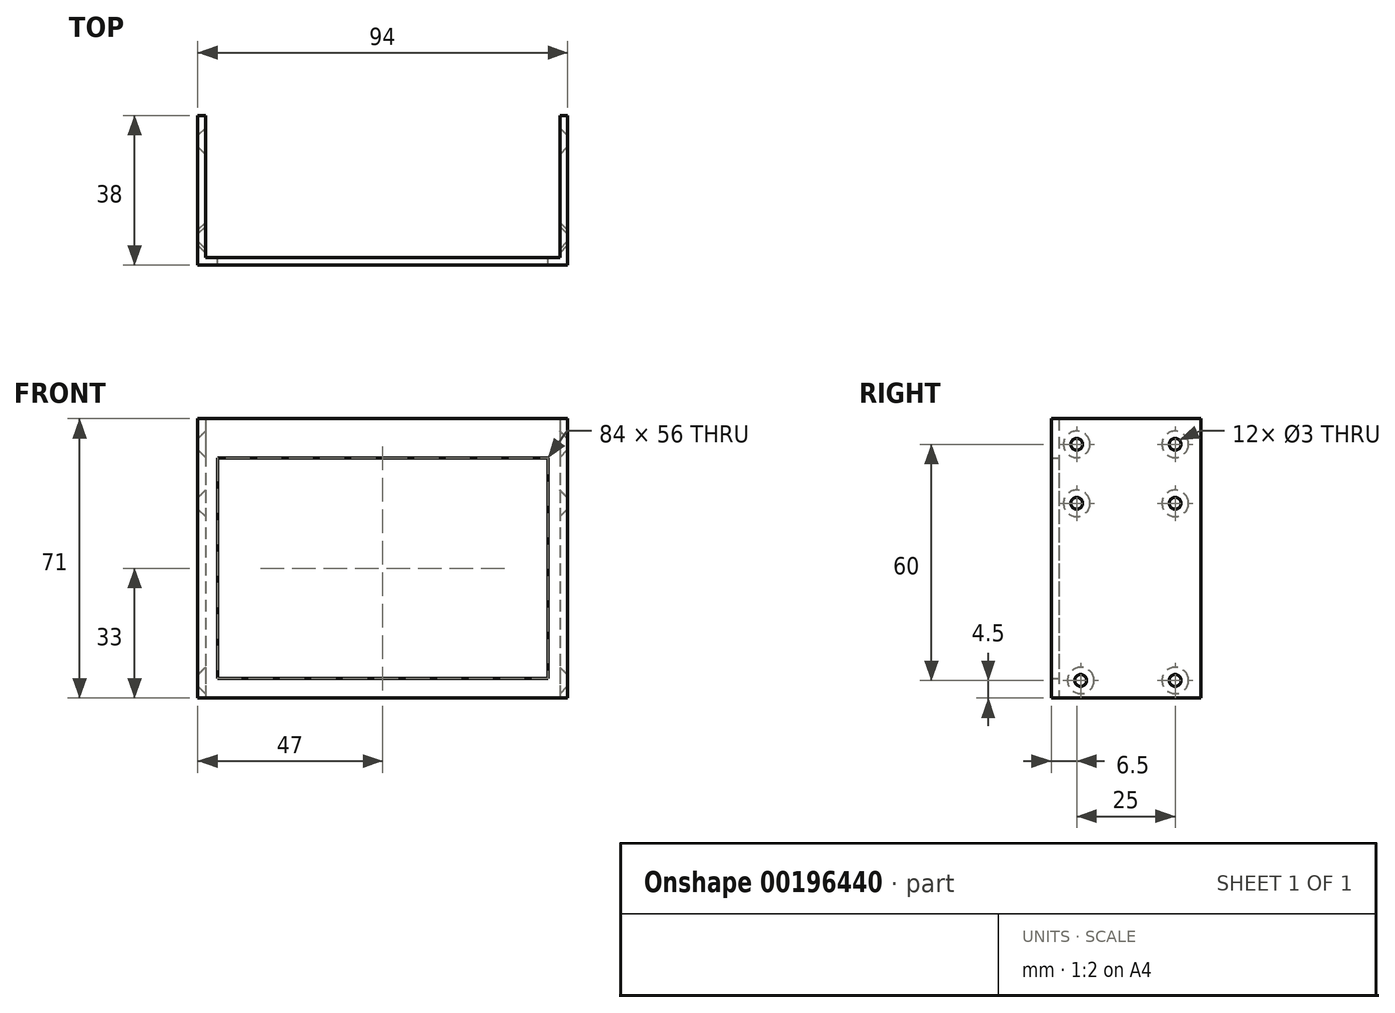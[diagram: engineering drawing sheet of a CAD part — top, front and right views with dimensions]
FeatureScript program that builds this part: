
annotation { "Feature Type Name" : "Feature", "Feature Type Description" : "" }
export const myFeature = defineFeature(function(context is Context, id is Id, definition is map)
    precondition{}
    {
        {
            var Q0;
            Q0=qCreatedBy(makeId("Front.planeOp"),FACE);
            var sketch = newSketch(context, id + "F0", { "sketchPlane" : qUnion([Q0])});
            skLineSegment(sketch, "E0.bottom", {"start": v(47, 35.5) * mm, "end": v(-47, 35.5) * mm});
            skLineSegment(sketch, "E0.top", {"start": v(47, -35.5) * mm, "end": v(-47, -35.5) * mm});
            skLineSegment(sketch, "E0.left", {"start": v(47, 35.5) * mm, "end": v(47, -35.5) * mm});
            skLineSegment(sketch, "E0.right", {"start": v(-47, 35.5) * mm, "end": v(-47, -35.5) * mm});
            skPoint(sketch, "E0.middle", {"position": v(0, 0) * mm});
            skLineSegment(sketch, "E1.bottom", {"start": v(42, 25.5) * mm, "end": v(-42, 25.5) * mm});
            skLineSegment(sketch, "E1.top", {"start": v(42, -30.5) * mm, "end": v(-42, -30.5) * mm});
            skLineSegment(sketch, "E1.left", {"start": v(42, 25.5) * mm, "end": v(42, -30.5) * mm});
            skLineSegment(sketch, "E1.right", {"start": v(-42, 25.5) * mm, "end": v(-42, -30.5) * mm});
            skPoint(sketch, "E1.middle", {"position": v(0, -2.5) * mm});
            skSolve(sketch);
        }
        {
            var Q0;
            Q0=qSketchRegion(id+"F0",true);
            extrude(context, id + "F1", {"entities" : qUnion([Q0]), "endBound" : BoundingType.SYMMETRIC, "depth" : 2 * mm});
        }
        {
            var Q0;
            Q0=makeQuery(id+"F1.opExtrude","CAP_FACE",FACE,{"disambiguationData":[OSD([sQuery(id+"F0.wireOp",EDGE,"E0.bottom"),sQuery(id+"F0.wireOp",EDGE,"E0.top"),sQuery(id+"F0.wireOp",EDGE,"E0.left"),sQuery(id+"F0.wireOp",EDGE,"E0.right"),sQuery(id+"F0.wireOp",EDGE,"SgeA5SFv-ycm6-KkIP-0Kqd-vPRJc91bn5sW.bottom"),sQuery(id+"F0.wireOp",EDGE,"SgeA5SFv-ycm6-KkIP-0Kqd-vPRJc91bn5sW.top"),sQuery(id+"F0.wireOp",EDGE,"SgeA5SFv-ycm6-KkIP-0Kqd-vPRJc91bn5sW.left"),sQuery(id+"F0.wireOp",EDGE,"SgeA5SFv-ycm6-KkIP-0Kqd-vPRJc91bn5sW.right")])],"isStart":true});
            var sketch = newSketch(context, id + "F2", { "sketchPlane" : qUnion([Q0])});
            skLineSegment(sketch, "E2.bottom", {"start": v(-47, 35.5) * mm, "end": v(-45, 35.5) * mm});
            skLineSegment(sketch, "E2.top", {"start": v(-47, -35.5) * mm, "end": v(-45, -35.5) * mm});
            skLineSegment(sketch, "E2.left", {"start": v(-47, 35.5) * mm, "end": v(-47, -35.5) * mm});
            skLineSegment(sketch, "E2.right", {"start": v(-45, 35.5) * mm, "end": v(-45, -35.5) * mm});
            skLineSegment(sketch, "E3.bottom", {"start": v(47, 35.5) * mm, "end": v(45, 35.5) * mm});
            skLineSegment(sketch, "E3.top", {"start": v(47, -35.5) * mm, "end": v(45, -35.5) * mm});
            skLineSegment(sketch, "E3.left", {"start": v(47, 35.5) * mm, "end": v(47, -35.5) * mm});
            skLineSegment(sketch, "E3.right", {"start": v(45, 35.5) * mm, "end": v(45, -35.5) * mm});
            skSolve(sketch);
        }
        {
            var Q0;
            Q0=qSketchRegion(id+"F2",true);
            extrude(context, id + "F3", {"entities" : qUnion([Q0]), "operationType" : NewBodyOperationType.ADD, "depth" : 36 * mm});
        }
        {
            var Q0;
            Q0=makeQuery(id+"F3.boolean.opBoolean","MERGE",FACE,{"derivedFrom":[makeQuery(id+"F1.opExtrude","SWEPT_FACE",FACE,{"disambiguationData":[OSD([sQuery(id+"F0.wireOp",EDGE,"E0.right")])]}),makeQuery(id+"F3.opExtrude","SWEPT_FACE",FACE,{"disambiguationData":[OSD([sQuery(id+"F2.wireOp",EDGE,"E3.left")])]})]});
            var sketch = newSketch(context, id + "F4", { "sketchPlane" : qUnion([Q0])});
            skCircle(sketch, "E4", {"center": v(-30.5, -31) * mm, "radius": 1.5 * mm});
            skCircle(sketch, "E5", {"center": v(-6.5, -31) * mm, "radius": 1.5 * mm});
            skCircle(sketch, "E6", {"center": v(-30.5, 29) * mm, "radius": 1.5 * mm});
            skCircle(sketch, "E7", {"center": v(-5.5, 29) * mm, "radius": 1.5 * mm});
            skLineSegment(sketch, "E8", {"start": v(-30.5, 29) * mm, "end": v(-30.5, -31) * mm, "construction": true});
            skCircle(sketch, "E9", {"center": v(-30.5, 14) * mm, "radius": 1.5 * mm});
            skCircle(sketch, "E10", {"center": v(-5.5, 14) * mm, "radius": 1.5 * mm});
            skSolve(sketch);
        }
        {
            var Q0;
            Q0=qSketchRegion(id+"F4",true);
            extrude(context, id + "F5", {"entities" : qUnion([Q0]), "operationType" : NewBodyOperationType.REMOVE, "oppositeDirection" : true, "depth" : 100 * mm});
        }
        {
            var Q0;
            Q0=makeQuery(id+"F5.boolean.opBoolean","INTERSECT",EDGE,{"derivedFrom":[makeQuery(id+"F3.opExtrude","SWEPT_FACE",FACE,{"disambiguationData":[OSD([sQuery(id+"F2.wireOp",EDGE,"E3.right")])]}),makeQuery(id+"F5.opExtrude","SWEPT_FACE",FACE,{"disambiguationData":[OSD([sQuery(id+"F4.wireOp",EDGE,"E6")])]})]});
            var Q1;
            Q1=makeQuery(id+"F5.boolean.opBoolean","INTERSECT",EDGE,{"derivedFrom":[makeQuery(id+"F3.opExtrude","SWEPT_FACE",FACE,{"disambiguationData":[OSD([sQuery(id+"F2.wireOp",EDGE,"E3.right")])]}),makeQuery(id+"F5.opExtrude","SWEPT_FACE",FACE,{"disambiguationData":[OSD([sQuery(id+"F4.wireOp",EDGE,"E9")])]})]});
            var Q2;
            Q2=makeQuery(id+"F5.boolean.opBoolean","INTERSECT",EDGE,{"derivedFrom":[makeQuery(id+"F3.opExtrude","SWEPT_FACE",FACE,{"disambiguationData":[OSD([sQuery(id+"F2.wireOp",EDGE,"E3.right")])]}),makeQuery(id+"F5.opExtrude","SWEPT_FACE",FACE,{"disambiguationData":[OSD([sQuery(id+"F4.wireOp",EDGE,"E7")])]})]});
            var Q3;
            Q3=makeQuery(id+"F5.boolean.opBoolean","INTERSECT",EDGE,{"derivedFrom":[makeQuery(id+"F3.opExtrude","SWEPT_FACE",FACE,{"disambiguationData":[OSD([sQuery(id+"F2.wireOp",EDGE,"E2.right")])]}),makeQuery(id+"F5.opExtrude","SWEPT_FACE",FACE,{"disambiguationData":[OSD([sQuery(id+"F4.wireOp",EDGE,"E7")])]})]});
            var Q4;
            Q4=makeQuery(id+"F5.boolean.opBoolean","INTERSECT",EDGE,{"derivedFrom":[makeQuery(id+"F3.opExtrude","SWEPT_FACE",FACE,{"disambiguationData":[OSD([sQuery(id+"F2.wireOp",EDGE,"E2.right")])]}),makeQuery(id+"F5.opExtrude","SWEPT_FACE",FACE,{"disambiguationData":[OSD([sQuery(id+"F4.wireOp",EDGE,"E10")])]})]});
            var Q5;
            Q5=makeQuery(id+"F5.boolean.opBoolean","INTERSECT",EDGE,{"derivedFrom":[makeQuery(id+"F3.opExtrude","SWEPT_FACE",FACE,{"disambiguationData":[OSD([sQuery(id+"F2.wireOp",EDGE,"E2.right")])]}),makeQuery(id+"F5.opExtrude","SWEPT_FACE",FACE,{"disambiguationData":[OSD([sQuery(id+"F4.wireOp",EDGE,"E6")])]})]});
            var Q6;
            Q6=makeQuery(id+"F5.boolean.opBoolean","INTERSECT",EDGE,{"derivedFrom":[makeQuery(id+"F3.opExtrude","SWEPT_FACE",FACE,{"disambiguationData":[OSD([sQuery(id+"F2.wireOp",EDGE,"E2.right")])]}),makeQuery(id+"F5.opExtrude","SWEPT_FACE",FACE,{"disambiguationData":[OSD([sQuery(id+"F4.wireOp",EDGE,"E9")])]})]});
            var Q7;
            Q7=makeQuery(id+"F5.boolean.opBoolean","INTERSECT",EDGE,{"derivedFrom":[makeQuery(id+"F3.opExtrude","SWEPT_FACE",FACE,{"disambiguationData":[OSD([sQuery(id+"F2.wireOp",EDGE,"E3.right")])]}),makeQuery(id+"F5.opExtrude","SWEPT_FACE",FACE,{"disambiguationData":[OSD([sQuery(id+"F4.wireOp",EDGE,"E10")])]})]});
            var Q8;
            Q8=makeQuery(id+"F5.boolean.opBoolean","INTERSECT",EDGE,{"derivedFrom":[makeQuery(id+"F3.opExtrude","SWEPT_FACE",FACE,{"disambiguationData":[OSD([sQuery(id+"F2.wireOp",EDGE,"E2.right")])]}),makeQuery(id+"F5.opExtrude","SWEPT_FACE",FACE,{"disambiguationData":[OSD([sQuery(id+"F4.wireOp",EDGE,"E5")])]})]});
            var Q9;
            Q9=makeQuery(id+"F5.boolean.opBoolean","INTERSECT",EDGE,{"derivedFrom":[makeQuery(id+"F3.opExtrude","SWEPT_FACE",FACE,{"disambiguationData":[OSD([sQuery(id+"F2.wireOp",EDGE,"E2.right")])]}),makeQuery(id+"F5.opExtrude","SWEPT_FACE",FACE,{"disambiguationData":[OSD([sQuery(id+"F4.wireOp",EDGE,"E4")])]})]});
            var Q10;
            Q10=makeQuery(id+"F5.boolean.opBoolean","INTERSECT",EDGE,{"derivedFrom":[makeQuery(id+"F3.opExtrude","SWEPT_FACE",FACE,{"disambiguationData":[OSD([sQuery(id+"F2.wireOp",EDGE,"E3.right")])]}),makeQuery(id+"F5.opExtrude","SWEPT_FACE",FACE,{"disambiguationData":[OSD([sQuery(id+"F4.wireOp",EDGE,"E5")])]})]});
            var Q11;
            Q11=makeQuery(id+"F5.boolean.opBoolean","INTERSECT",EDGE,{"derivedFrom":[makeQuery(id+"F3.opExtrude","SWEPT_FACE",FACE,{"disambiguationData":[OSD([sQuery(id+"F2.wireOp",EDGE,"E3.right")])]}),makeQuery(id+"F5.opExtrude","SWEPT_FACE",FACE,{"disambiguationData":[OSD([sQuery(id+"F4.wireOp",EDGE,"E4")])]})]});
            chamfer(context, id + "F6", {"entities" : qUnion([Q0, Q1, Q2, Q3, Q4, Q5, Q6, Q7, Q8, Q9, Q10, Q11]), "width" : 1.87 * mm, "tangentPropagation" : true});
        }
    });
